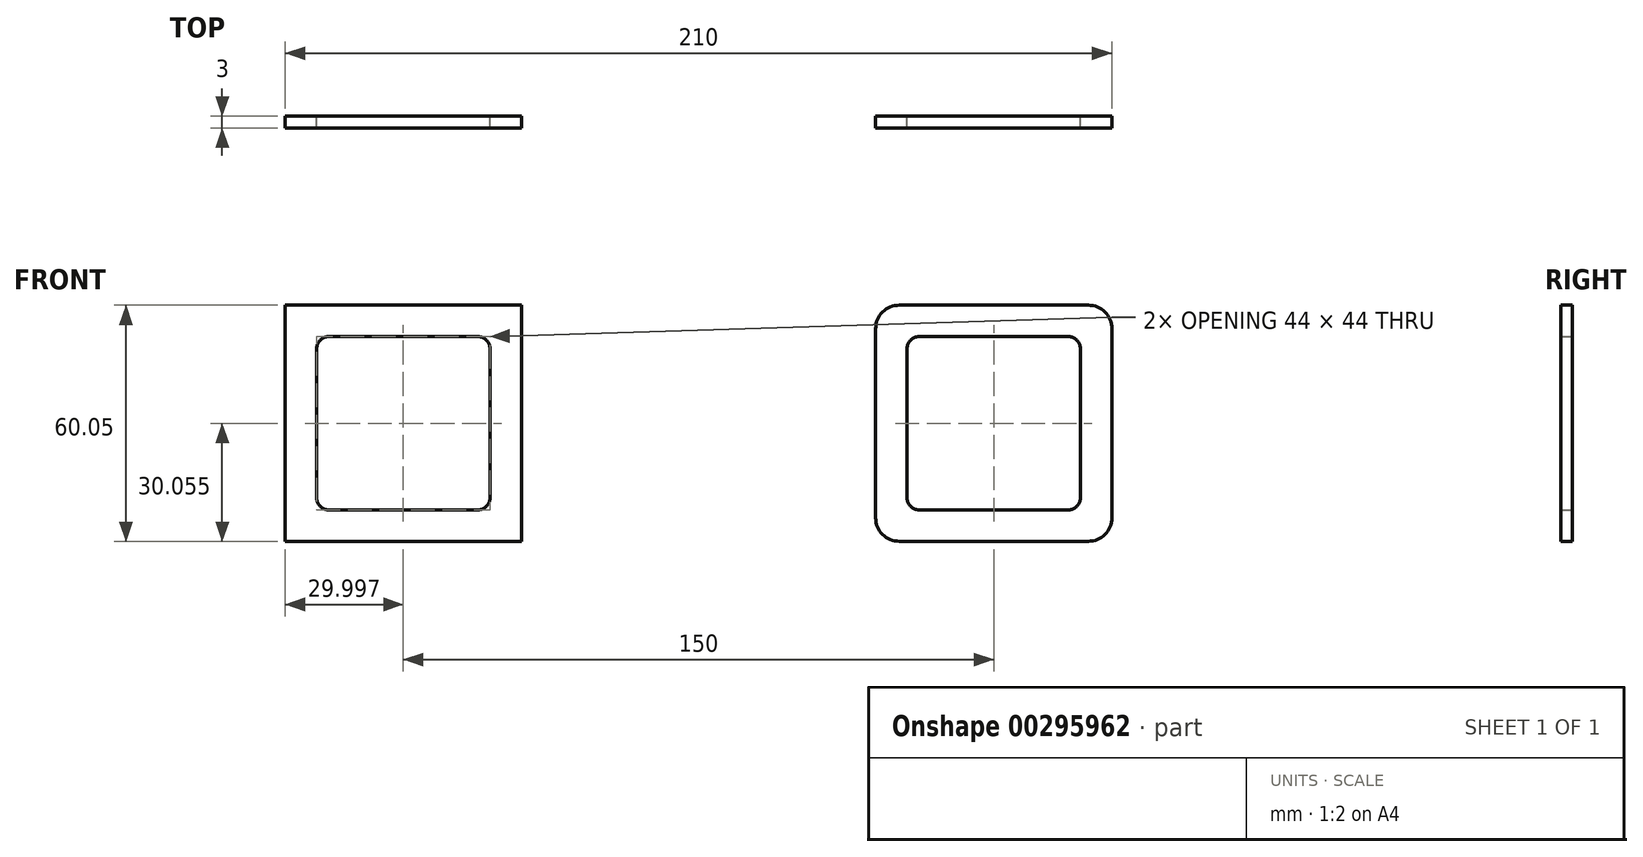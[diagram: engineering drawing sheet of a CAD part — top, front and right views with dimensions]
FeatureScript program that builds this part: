
annotation { "Feature Type Name" : "Feature", "Feature Type Description" : "" }
export const myFeature = defineFeature(function(context is Context, id is Id, definition is map)
    precondition{}
    {
        {
            var Q0;
            Q0=qCreatedBy(makeId("Front.planeOp"),FACE);
            var sketch = newSketch(context, id + "F0", { "sketchPlane" : qUnion([Q0])});
            skLineSegment(sketch, "E0.bottom", {"start": v(50.99, 29.08) * mm, "end": v(98.99, 29.08) * mm});
            skLineSegment(sketch, "E0.top", {"start": v(50.99, -30.92) * mm, "end": v(98.99, -30.92) * mm});
            skLineSegment(sketch, "E0.left", {"start": v(44.99, 23.08) * mm, "end": v(44.99, -24.92) * mm});
            skLineSegment(sketch, "E0.right", {"start": v(104.99, 23.08) * mm, "end": v(104.99, -24.92) * mm});
            skLineSegment(sketch, "E1.bottom", {"start": v(55.99, 21.08) * mm, "end": v(93.99, 21.08) * mm});
            skLineSegment(sketch, "E1.top", {"start": v(55.99, -22.92) * mm, "end": v(93.99, -22.92) * mm});
            skLineSegment(sketch, "E1.left", {"start": v(52.99, 18.08) * mm, "end": v(52.99, -19.92) * mm});
            skLineSegment(sketch, "E1.right", {"start": v(96.99, 18.08) * mm, "end": v(96.99, -19.92) * mm});
            skPoint(sketch, "E2.visualSharp", {"position": v(44.99, 29.08) * mm});
            skArc(sketch, "E2.filletArc", {"start": v(50.99, 29.08) * mm, "mid": v(46.74, 27.33) * mm, "end": v(44.99, 23.08) * mm});
            skPoint(sketch, "E3.visualSharp", {"position": v(104.99, 29.08) * mm});
            skArc(sketch, "E3.filletArc", {"start": v(104.99, 23.08) * mm, "mid": v(103.23, 27.33) * mm, "end": v(98.99, 29.08) * mm});
            skPoint(sketch, "E4.visualSharp", {"position": v(44.99, -30.92) * mm});
            skArc(sketch, "E4.filletArc", {"start": v(44.99, -24.92) * mm, "mid": v(46.74, -29.16) * mm, "end": v(50.99, -30.92) * mm});
            skPoint(sketch, "E5.visualSharp", {"position": v(104.99, -30.92) * mm});
            skArc(sketch, "E5.filletArc", {"start": v(98.99, -30.92) * mm, "mid": v(103.23, -29.16) * mm, "end": v(104.99, -24.92) * mm});
            skPoint(sketch, "E6.visualSharp", {"position": v(52.99, -22.92) * mm});
            skArc(sketch, "E6.filletArc", {"start": v(52.99, -19.92) * mm, "mid": v(53.87, -22.04) * mm, "end": v(55.99, -22.92) * mm});
            skPoint(sketch, "E7.visualSharp", {"position": v(96.99, -22.92) * mm});
            skArc(sketch, "E7.filletArc", {"start": v(93.99, -22.92) * mm, "mid": v(96.1, -22.04) * mm, "end": v(96.99, -19.92) * mm});
            skPoint(sketch, "E8.visualSharp", {"position": v(96.99, 21.08) * mm});
            skArc(sketch, "E8.filletArc", {"start": v(96.99, 18.08) * mm, "mid": v(96.1, 20.2) * mm, "end": v(93.99, 21.08) * mm});
            skPoint(sketch, "E9.visualSharp", {"position": v(52.99, 21.08) * mm});
            skArc(sketch, "E9.filletArc", {"start": v(55.99, 21.08) * mm, "mid": v(53.87, 20.2) * mm, "end": v(52.99, 18.08) * mm});
            skLineSegment(sketch, "E10.MirrorCS", {"start": v(-105.01, 23.08) * mm, "end": v(-105.01, -24.92) * mm});
            skArc(sketch, "E11.MirrorCS", {"start": v(-105.01, 23.08) * mm, "mid": v(-103.26, 27.33) * mm, "end": v(-99.01, 29.08) * mm});
            skLineSegment(sketch, "E12.MirrorCS", {"start": v(-51.01, 29.08) * mm, "end": v(-99.01, 29.08) * mm});
            skLineSegment(sketch, "E13.MirrorCS", {"start": v(-56.01, 21.08) * mm, "end": v(-94.01, 21.08) * mm});
            skLineSegment(sketch, "E14.MirrorCS", {"start": v(-45.01, 23.08) * mm, "end": v(-45.01, -24.92) * mm});
            skLineSegment(sketch, "E15.MirrorCS", {"start": v(-51.01, -30.92) * mm, "end": v(-99.01, -30.92) * mm});
            skArc(sketch, "E16.MirrorCS", {"start": v(-45.01, -24.92) * mm, "mid": v(-46.77, -29.16) * mm, "end": v(-51.01, -30.92) * mm});
            skArc(sketch, "E17.MirrorCS", {"start": v(-99.01, -30.92) * mm, "mid": v(-103.26, -29.16) * mm, "end": v(-105.01, -24.92) * mm});
            skLineSegment(sketch, "E18.MirrorCS", {"start": v(-53.01, 18.08) * mm, "end": v(-53.01, -19.92) * mm});
            skLineSegment(sketch, "E19.MirrorCS", {"start": v(-56.01, -22.92) * mm, "end": v(-94.01, -22.92) * mm});
            skLineSegment(sketch, "E20.MirrorCS", {"start": v(-97.01, 18.08) * mm, "end": v(-97.01, -19.92) * mm});
            skArc(sketch, "E21.MirrorCS", {"start": v(-56.01, 21.08) * mm, "mid": v(-53.9, 20.2) * mm, "end": v(-53.01, 18.08) * mm});
            skArc(sketch, "E22.MirrorCS", {"start": v(-97.01, 18.08) * mm, "mid": v(-96.13, 20.2) * mm, "end": v(-94.01, 21.08) * mm});
            skArc(sketch, "E23.MirrorCS", {"start": v(-53.01, -19.92) * mm, "mid": v(-53.9, -22.04) * mm, "end": v(-56.01, -22.92) * mm});
            skArc(sketch, "E24.MirrorCS", {"start": v(-94.01, -22.92) * mm, "mid": v(-96.13, -22.04) * mm, "end": v(-97.01, -19.92) * mm});
            skArc(sketch, "E25.MirrorCS", {"start": v(-51.01, 29.08) * mm, "mid": v(-46.77, 27.33) * mm, "end": v(-45.01, 23.08) * mm});
            skLineSegment(sketch, "E26.bottom", {"start": v(-105.01, 29.08) * mm, "end": v(-45.01, 29.08) * mm});
            skLineSegment(sketch, "E26.top", {"start": v(-105.01, -30.97) * mm, "end": v(-45.01, -30.97) * mm});
            skLineSegment(sketch, "E26.left", {"start": v(-105.01, 29.08) * mm, "end": v(-105.01, -30.97) * mm});
            skLineSegment(sketch, "E26.right", {"start": v(-45.01, 29.08) * mm, "end": v(-45.01, -30.97) * mm});
            skSolve(sketch);
        }
        {
            var Q0;
            Q0 = qSketchRegion(id + "F0", true);
            extrude(context, id + "F1", {"entities" : qUnion([Q0]), "depth" : 3 * mm});
        }
    });
